# Revit family: oventrop_regudis-w-htf_1341130-32rfa
name_source: partatom
category: Оборудование
revit_build: Autodesk Revit 2017 (Build: 20160225_1515(x64)
units: mm (PartAtom-declared; Revit-internal decimal feet)

## family parameters
Всегда вертикально = Да
Заголовок OmniClass = Climate Control (HVAC)
На основе рабочей плоскости = Нет
Номер OmniClass = 23.75.00.00
Общий = Нет
При загрузке вырезать с полостями = Да
Размер круглого соединителя = Использовать диаметр
Тип детали = Нормальный
Точка расчета площади = Нет

## types (3) — shared parameters
Connection Diameter = 19 мм
Connection Set Length = 31 мм
Custom = Нет
Depth = 110 мм
EMCS Version = 2.0
ETIM Article Class = EC011394
Family Version = 10.14
Grey = Color RGB 140-140-140
Height = 655 мм
IFCExportAs = IfcHeatExchangerType
IFCExportType = NOTDEFINED
Length = 565 мм
MEPcontent Class = HEAT_EXCHANGER
Manufacturer URL = http://www.oventrop.com
Primary Volume Flow = 0.0 л/с
Product Line = Oventrop
Revit Version = 2015
Secondary Volume Flow = 0.0 л/с
Use Nominal Diameter = Да
Voltage = 230 В
White = Color RAL 9010
Изготовитель = Oventrop

## per-type parameters (varying)
| type | Article Description | GTIN | Manufacturer Art. No. | Power | URL | Описание |
| 12 l/min | Dwelling station with constant temperature circuit, hot potable water performance range - 12 l/min | 4026755383140 | 1341130 | 29000 Вт | http://file-system.ru | Dwelling station with constant temperature circuit, hot potable water performance range - 12 l/min |
| 15 l/min | Dwelling station with constant temperature circuit, hot potable water performance range - 15 l/min | 4026755383157 | 1341131 | 36000 Вт | www.stabiplan.com | Dwelling station with constant temperature circuit, hot potable water performance range - 15 l/min |
| 17 l/min | Dwelling station with constant temperature circuit, hot potable water performance range - 17 l/min | 4026755383164 | 1341132 | 42000 Вт | www.stabiplan.com | Dwelling station with constant temperature circuit, hot potable water performance range - 17 l/min |

note: column(s) folded — value = type name in every type: Article Type, Группа модели

## geometry (parser evidence)
native form markers: Sweep x9
no freeform markers — native parametric forms only
